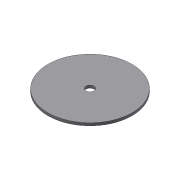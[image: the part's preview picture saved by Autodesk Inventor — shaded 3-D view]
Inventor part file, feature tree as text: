
AUTODESK INVENTOR PART (.ipt)
format: ipt  version: 2015 (Build 190159000, 159)  size: 72,192 bytes
history: native  units: mm
features: extrude x1, sketch x1
ambient origin geometry x8: Origin, YZ Plane, XZ Plane, XY Plane, X Axis, Y Axis, Z Axis, Center Point
bodies: Solid1 (feature_tree)
feature tree (2):
  extrude  "Extrusion1"  Depth=3.0mm
  sketch  "Sketch1"  dims[d0=9.18mm d1=94.0mm d2=3.0mm d3=0.0mm]
